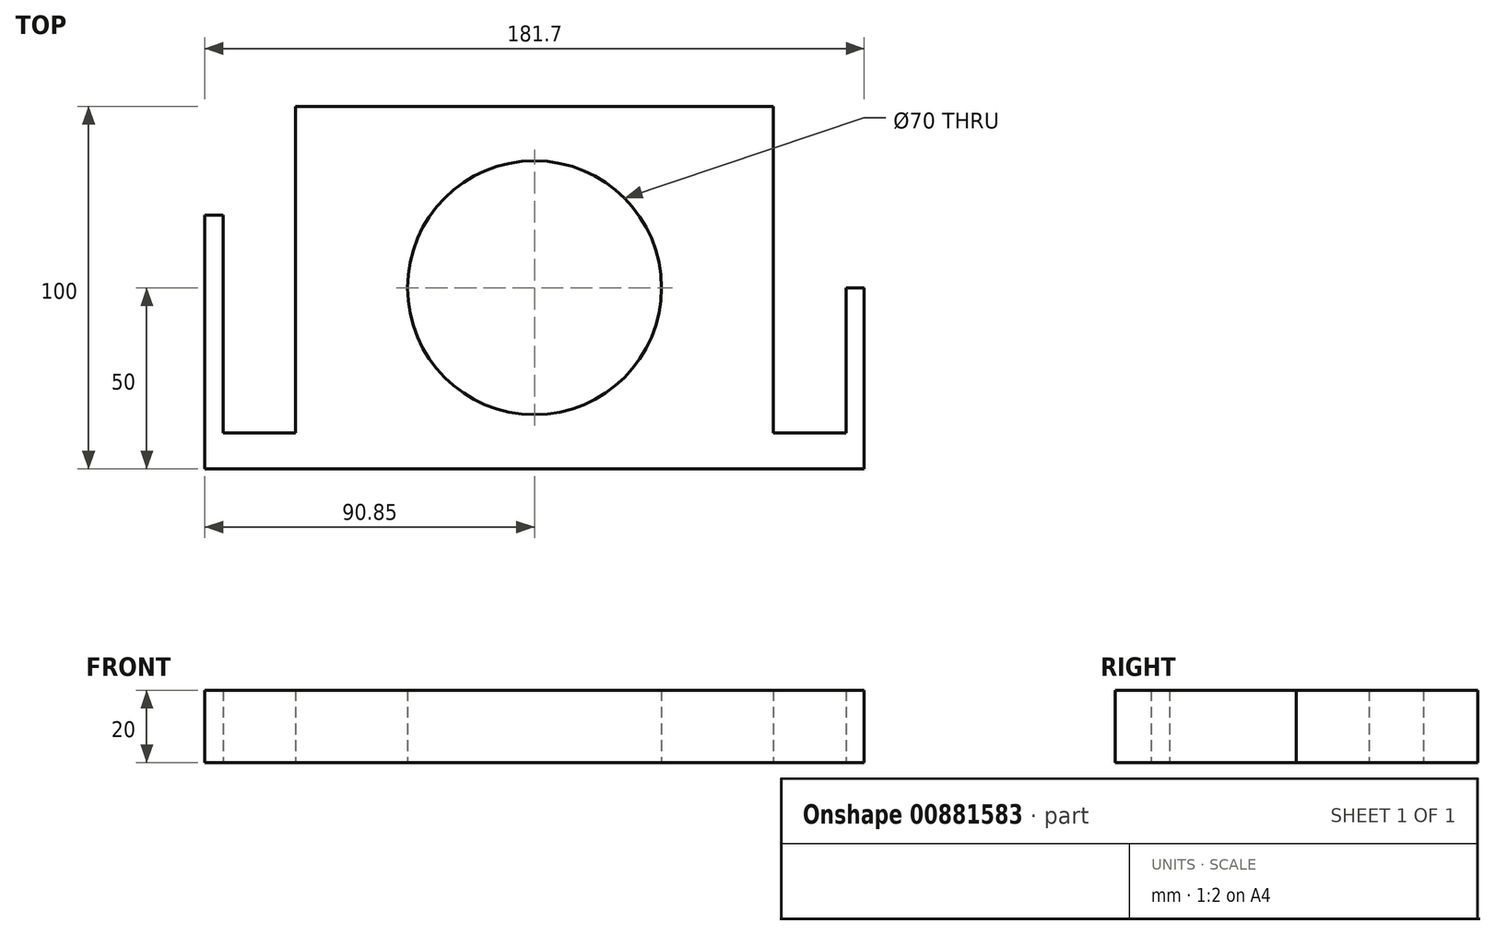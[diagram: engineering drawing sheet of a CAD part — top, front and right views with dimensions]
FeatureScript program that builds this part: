
annotation { "Feature Type Name" : "Feature", "Feature Type Description" : "" }
export const myFeature = defineFeature(function(context is Context, id is Id, definition is map)
    precondition{}
    {
        {
            var Q0;
            Q0=qCreatedBy(makeId("Top.planeOp"),FACE);
            var sketch = newSketch(context, id + "F0", { "sketchPlane" : qUnion([Q0])});
            skLineSegment(sketch, "E0", {"start": v(-109.15, 0) * mm, "end": v(90.85, 0) * mm});
            skLineSegment(sketch, "E1", {"start": v(90.85, 0) * mm, "end": v(90.85, 50) * mm});
            skLineSegment(sketch, "E2", {"start": v(85.85, 50) * mm, "end": v(85.85, 10) * mm});
            skLineSegment(sketch, "E3", {"start": v(85.85, 10) * mm, "end": v(75.85, 10) * mm});
            skLineSegment(sketch, "E4", {"start": v(75.85, 10) * mm, "end": v(65.85, 10) * mm});
            skLineSegment(sketch, "E5", {"start": v(65.85, 10) * mm, "end": v(65.85, 70) * mm});
            skLineSegment(sketch, "E6.MirrorCS", {"start": v(-65.85, 10) * mm, "end": v(-65.85, 70) * mm});
            skLineSegment(sketch, "E7.MirrorCS", {"start": v(-75.85, 10) * mm, "end": v(-65.85, 10) * mm});
            skLineSegment(sketch, "E8.MirrorCS", {"start": v(-85.85, 10) * mm, "end": v(-75.85, 10) * mm});
            skLineSegment(sketch, "E9.MirrorCS", {"start": v(-85.85, 50) * mm, "end": v(-85.85, 10) * mm});
            skLineSegment(sketch, "E10.MirrorCS", {"start": v(-90.85, 0) * mm, "end": v(-90.85, 50) * mm});
            skLineSegment(sketch, "E11", {"start": v(65.85, 70) * mm, "end": v(65.85, 90) * mm});
            skLineSegment(sketch, "E12", {"start": v(-65.85, 90) * mm, "end": v(-65.85, 70) * mm});
            skLineSegment(sketch, "E13", {"start": v(0, 0) * mm, "end": v(0, 50) * mm});
            skLineSegment(sketch, "E14.0", {"start": v(-90.85, 70) * mm, "end": v(-85.85, 70) * mm});
            skLineSegment(sketch, "E15.0", {"start": v(90.85, 50) * mm, "end": v(85.85, 50) * mm});
            skLineSegment(sketch, "E16.0", {"start": v(90.85, 70) * mm, "end": v(85.85, 70) * mm});
            skLineSegment(sketch, "E17", {"start": v(-90.85, 70) * mm, "end": v(-90.85, 50) * mm});
            skLineSegment(sketch, "E18", {"start": v(-85.85, 70) * mm, "end": v(-85.85, 50) * mm});
            skLineSegment(sketch, "E19", {"start": v(85.85, 70) * mm, "end": v(85.85, 50) * mm});
            skLineSegment(sketch, "E20", {"start": v(90.85, 70) * mm, "end": v(90.85, 50) * mm});
            skLineSegment(sketch, "E21.0", {"start": v(-65.85, 100) * mm, "end": v(65.85, 100) * mm});
            skLineSegment(sketch, "E22", {"start": v(-65.85, 100) * mm, "end": v(-65.85, 90) * mm});
            skLineSegment(sketch, "E23", {"start": v(65.85, 100) * mm, "end": v(65.85, 90) * mm});
            skCircle(sketch, "E24", {"center": v(0, 50) * mm, "radius": 35 * mm});
            skSolve(sketch);
        }
        {
            var Q0;
            {var subQ3=sQuery(id+"F0.wireOp",EDGE,"E1");Q0=makeQuery(id+"F0.imprint","IMPRINT",FACE,{"disambiguationData":[TD([[makeQuery(id+"F0.imprint","IMPRINT",EDGE,{"derivedFrom":subQ3}),1.0]])]});}
            extrude(context, id + "F1", {"entities" : qUnion([Q0]), "depth" : 20 * mm, "offsetDistance" : 25 * mm});
        }
    });
